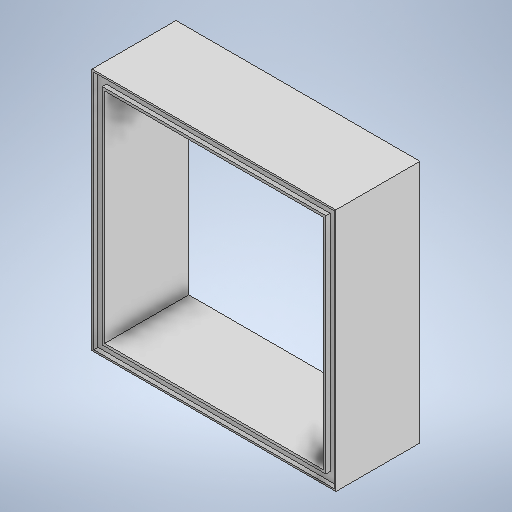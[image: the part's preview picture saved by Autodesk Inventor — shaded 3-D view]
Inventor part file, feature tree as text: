
AUTODESK INVENTOR PART (.ipt)
format: ipt  version: 2025.2 (Build 292293000, 293)  size: 243,200 bytes
history: native  units: mm
features: sketch x3, extrude x1, sweep x1
ambient origin geometry x8: Origin, YZ Plane, XZ Plane, XY Plane, X Axis, Y Axis, Z Axis, Center Point
bodies: Solid1 (feature_tree)
feature tree (5):
  sketch  "Sketch1"  dims[d0=29.0mm d1=29.0mm]
  extrude  "Extrusion1"  Depth=29.0mm
  sweep  "Sweep1"
  sketch  "Sketch5"  dims[d3=26.0mm d4=10.0mm d5=0.0mm]
  sketch  "Sketch6"  dims[d11=0.5mm d12=0.5mm d13=0.5mm d14=0.5mm d15=1.0mm d16=13.8mm d17=0.0mm d18=0.0mm]
